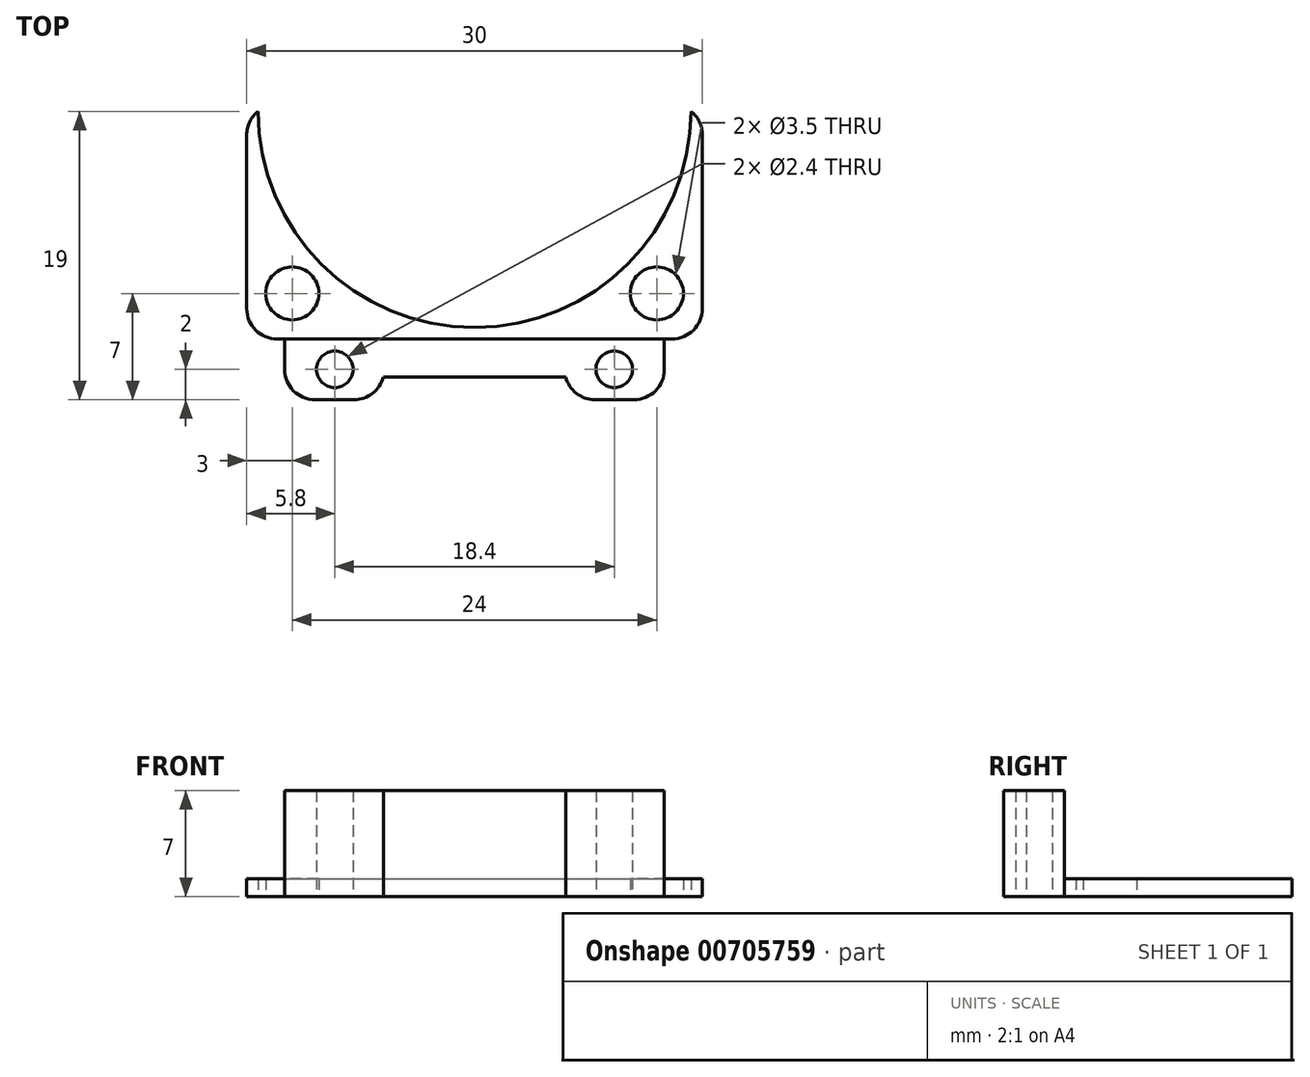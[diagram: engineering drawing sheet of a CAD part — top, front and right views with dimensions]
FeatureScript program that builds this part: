
annotation { "Feature Type Name" : "Feature", "Feature Type Description" : "" }
export const myFeature = defineFeature(function(context is Context, id is Id, definition is map)
    precondition{}
    {
        {
            var Q0;
            Q0=qCreatedBy(makeId("Top.planeOp"),FACE);
            var sketch = newSketch(context, id + "F0", { "sketchPlane" : qUnion([Q0])});
            skLineSegment(sketch, "E0.bottom", {"start": v(15, -15) * mm, "end": v(-15, -15) * mm});
            skLineSegment(sketch, "E0.left", {"start": v(15, -15) * mm, "end": v(15, 0) * mm});
            skLineSegment(sketch, "E0.right", {"start": v(-15, -15) * mm, "end": v(-15, 0) * mm});
            skPoint(sketch, "E0.middle", {"position": v(0, 0) * mm});
            skLineSegment(sketch, "E1.bottom", {"start": v(12, -12) * mm, "end": v(-12, -12) * mm, "construction": true});
            skLineSegment(sketch, "E1.top", {"start": v(12, 12) * mm, "end": v(-12, 12) * mm, "construction": true});
            skLineSegment(sketch, "E1.left", {"start": v(12, -12) * mm, "end": v(12, 10.45) * mm, "construction": true});
            skLineSegment(sketch, "E1.right", {"start": v(-12, -12) * mm, "end": v(-12, 12) * mm, "construction": true});
            skCircle(sketch, "E2", {"center": v(12, -12) * mm, "radius": 1.75 * mm});
            skCircle(sketch, "E3", {"center": v(-12, -12) * mm, "radius": 1.75 * mm});
            skLineSegment(sketch, "E4", {"start": v(-14.96, -19) * mm, "end": v(-6, -19) * mm, "construction": true});
            skLineSegment(sketch, "E5.bottom", {"start": v(-15, -15) * mm, "end": v(15, -15) * mm});
            skLineSegment(sketch, "E5.top", {"start": v(-6, -17.5) * mm, "end": v(6, -17.5) * mm});
            skLineSegment(sketch, "E6.bottom", {"start": v(-12.5, -15) * mm, "end": v(12.5, -15) * mm});
            skLineSegment(sketch, "E6.top", {"start": v(-12.5, -19) * mm, "end": v(-6, -19) * mm});
            skLineSegment(sketch, "E6.left", {"start": v(-12.5, -15) * mm, "end": v(-12.5, -19) * mm});
            skLineSegment(sketch, "E6.right", {"start": v(12.5, -15) * mm, "end": v(12.5, -19) * mm});
            skLineSegment(sketch, "E7.bottom", {"start": v(-6, -15) * mm, "end": v(6, -15) * mm});
            skLineSegment(sketch, "E7.left", {"start": v(-6, -15) * mm, "end": v(-6, -19) * mm});
            skLineSegment(sketch, "E7.right", {"start": v(6, -15) * mm, "end": v(6, -19) * mm});
            skPoint(sketch, "E5.right.end.orphan", {"position": v(15, -17.5) * mm});
            skLineSegment(sketch, "E8.trimOffspring", {"start": v(6, -19) * mm, "end": v(15.77, -19) * mm, "construction": true});
            skLineSegment(sketch, "E9.trimOffspring", {"start": v(6, -19) * mm, "end": v(12.5, -19) * mm});
            skLineSegment(sketch, "E10", {"start": v(-13.8, -17) * mm, "end": v(14.7, -17) * mm, "construction": true});
            skLineSegment(sketch, "E11", {"start": v(-9.2, -15) * mm, "end": v(-9.2, -21.94) * mm, "construction": true});
            skLineSegment(sketch, "E12", {"start": v(9.2, -15) * mm, "end": v(9.2, -21.94) * mm, "construction": true});
            skCircle(sketch, "E13", {"center": v(-9.2, -17) * mm, "radius": 1.2 * mm});
            skCircle(sketch, "E14", {"center": v(9.2, -17) * mm, "radius": 1.2 * mm});
            skLineSegment(sketch, "E15", {"start": v(-15, 0) * mm, "end": v(-14.25, 0) * mm});
            skLineSegment(sketch, "E16", {"start": v(14.25, 0) * mm, "end": v(15, 0) * mm});
            skPoint(sketch, "E16.startSnap0", {"position": v(12, 0) * mm});
            skArc(sketch, "E17.trimOffspring", {"start": v(-14.25, 0) * mm, "mid": v(0, -14.25) * mm, "end": v(14.25, 0) * mm});
            skPoint(sketch, "E0.top.end.orphan", {"position": v(-15, 15) * mm});
            skPoint(sketch, "E0.top.start.orphan", {"position": v(15, 15) * mm});
            skSolve(sketch);
        }
        {
            var Q0;
            Q0=makeQuery(id+"F0.imprint","IMPRINT",FACE,{"disambiguationData":[TD([[makeQuery(id+"F0.imprint","IMPRINT",EDGE,{"derivedFrom":sQuery(id+"F0.wireOp",EDGE,"E0.top")}),1.0]])]});
            var Q1;
            {var subQ4=sQuery(id+"F0.wireOp",EDGE,"E6.top");Q1=makeQuery(id+"F0.imprint","IMPRINT",FACE,{"disambiguationData":[TD([[makeQuery(id+"F0.imprint","IMPRINT",EDGE,{"derivedFrom":subQ4}),1.0]])]});}
            var Q2;
            {var subQ0=sQuery(id+"F0.wireOp",EDGE,"E5.top");Q2=makeQuery(id+"F0.imprint","IMPRINT",FACE,{"disambiguationData":[TD([[makeQuery(id+"F0.imprint","IMPRINT",EDGE,{"derivedFrom":subQ0}),1.0]])]});}
            var Q3;
            {var subQ5=sQuery(id+"F0.wireOp",EDGE,"E6.right");Q3=makeQuery(id+"F0.imprint","IMPRINT",FACE,{"disambiguationData":[TD([[makeQuery(id+"F0.imprint","IMPRINT",EDGE,{"derivedFrom":subQ5}),-1.0]])]});}
            var Q4;
            {var subQ5=sQuery(id+"F0.wireOp",EDGE,"E0.left");Q4=makeQuery(id+"F0.imprint","IMPRINT",FACE,{"disambiguationData":[TD([[makeQuery(id+"F0.imprint","IMPRINT",EDGE,{"derivedFrom":subQ5}),1.0]])]});}
            extrude(context, id + "F1", {"entities" : qUnion([Q0, Q1, Q2, Q3, Q4]), "depth" : 1.2 * mm, "offsetDistance" : 25 * mm});
        }
        {
            var Q0;
            {var subQ0=sQuery(id+"F0.wireOp",EDGE,"E5.top");Q0=makeQuery(id+"F0.imprint","IMPRINT",FACE,{"disambiguationData":[TD([[makeQuery(id+"F0.imprint","IMPRINT",EDGE,{"derivedFrom":subQ0}),1.0]])]});}
            var Q1;
            {var subQ4=sQuery(id+"F0.wireOp",EDGE,"E6.top");Q1=makeQuery(id+"F0.imprint","IMPRINT",FACE,{"disambiguationData":[TD([[makeQuery(id+"F0.imprint","IMPRINT",EDGE,{"derivedFrom":subQ4}),1.0]])]});}
            var Q2;
            {var subQ5=sQuery(id+"F0.wireOp",EDGE,"E6.right");Q2=makeQuery(id+"F0.imprint","IMPRINT",FACE,{"disambiguationData":[TD([[makeQuery(id+"F0.imprint","IMPRINT",EDGE,{"derivedFrom":subQ5}),-1.0]])]});}
            extrude(context, id + "F2", {"entities" : qUnion([Q0, Q1, Q2]), "operationType" : NewBodyOperationType.ADD, "depth" : 7 * mm});
        }
        {
            var Q0;
            {var subQ0=sQuery(id+"F0.wireOp",EDGE,"E6.left");var subQ1=sQuery(id+"F0.wireOp",EDGE,"E6.top");Q0=makeQuery(id+"F2.boolean.opBoolean","MERGE",EDGE,{"derivedFrom":[makeQuery(id+"F1.opExtrude","SWEPT_EDGE",EDGE,{"disambiguationData":[OSD([subQ1,subQ0])]}),makeQuery(id+"F2.opExtrude","SWEPT_EDGE",EDGE,{"disambiguationData":[OSD([subQ1,subQ0])]})]});}
            var Q1;
            {var subQ0=sQuery(id+"F0.wireOp",EDGE,"E9.trimOffspring");var subQ1=sQuery(id+"F0.wireOp",EDGE,"E6.right");Q1=makeQuery(id+"F2.boolean.opBoolean","MERGE",EDGE,{"derivedFrom":[makeQuery(id+"F1.opExtrude","SWEPT_EDGE",EDGE,{"disambiguationData":[OSD([subQ1,subQ0])]}),makeQuery(id+"F2.opExtrude","SWEPT_EDGE",EDGE,{"disambiguationData":[OSD([subQ1,subQ0])]})]});}
            var Q2;
            {var subQ0=sQuery(id+"F0.wireOp",EDGE,"E7.left");var subQ1=sQuery(id+"F0.wireOp",EDGE,"E6.top");Q2=makeQuery(id+"F2.boolean.opBoolean","MERGE",EDGE,{"derivedFrom":[makeQuery(id+"F1.opExtrude","SWEPT_EDGE",EDGE,{"disambiguationData":[OSD([subQ1,subQ0])]}),makeQuery(id+"F2.opExtrude","SWEPT_EDGE",EDGE,{"disambiguationData":[OSD([subQ1,subQ0])]})]});}
            var Q3;
            {var subQ0=sQuery(id+"F0.wireOp",EDGE,"E9.trimOffspring");var subQ1=sQuery(id+"F0.wireOp",EDGE,"E7.right");Q3=makeQuery(id+"F2.boolean.opBoolean","MERGE",EDGE,{"derivedFrom":[makeQuery(id+"F1.opExtrude","SWEPT_EDGE",EDGE,{"disambiguationData":[OSD([subQ1,subQ0])]}),makeQuery(id+"F2.opExtrude","SWEPT_EDGE",EDGE,{"disambiguationData":[OSD([subQ1,subQ0])]})]});}
            var Q4;
            Q4=makeQuery(id+"F1.opExtrude","SWEPT_EDGE",EDGE,{"disambiguationData":[OSD([sQuery(id+"F0.wireOp",EDGE,"E0.left"),sQuery(id+"F0.wireOp",EDGE,"E5.bottom")])]});
            var Q5;
            Q5=makeQuery(id+"F1.opExtrude","SWEPT_EDGE",EDGE,{"disambiguationData":[OSD([sQuery(id+"F0.wireOp",EDGE,"E0.right"),sQuery(id+"F0.wireOp",EDGE,"E5.bottom")])]});
            fillet(context, id + "F3", {"entities" : qUnion([Q0, Q1, Q2, Q3, Q4, Q5]), "radius" : 2 * mm, "tangentPropagation" : true, "allowEdgeOverflow" : false});
        }
    });
